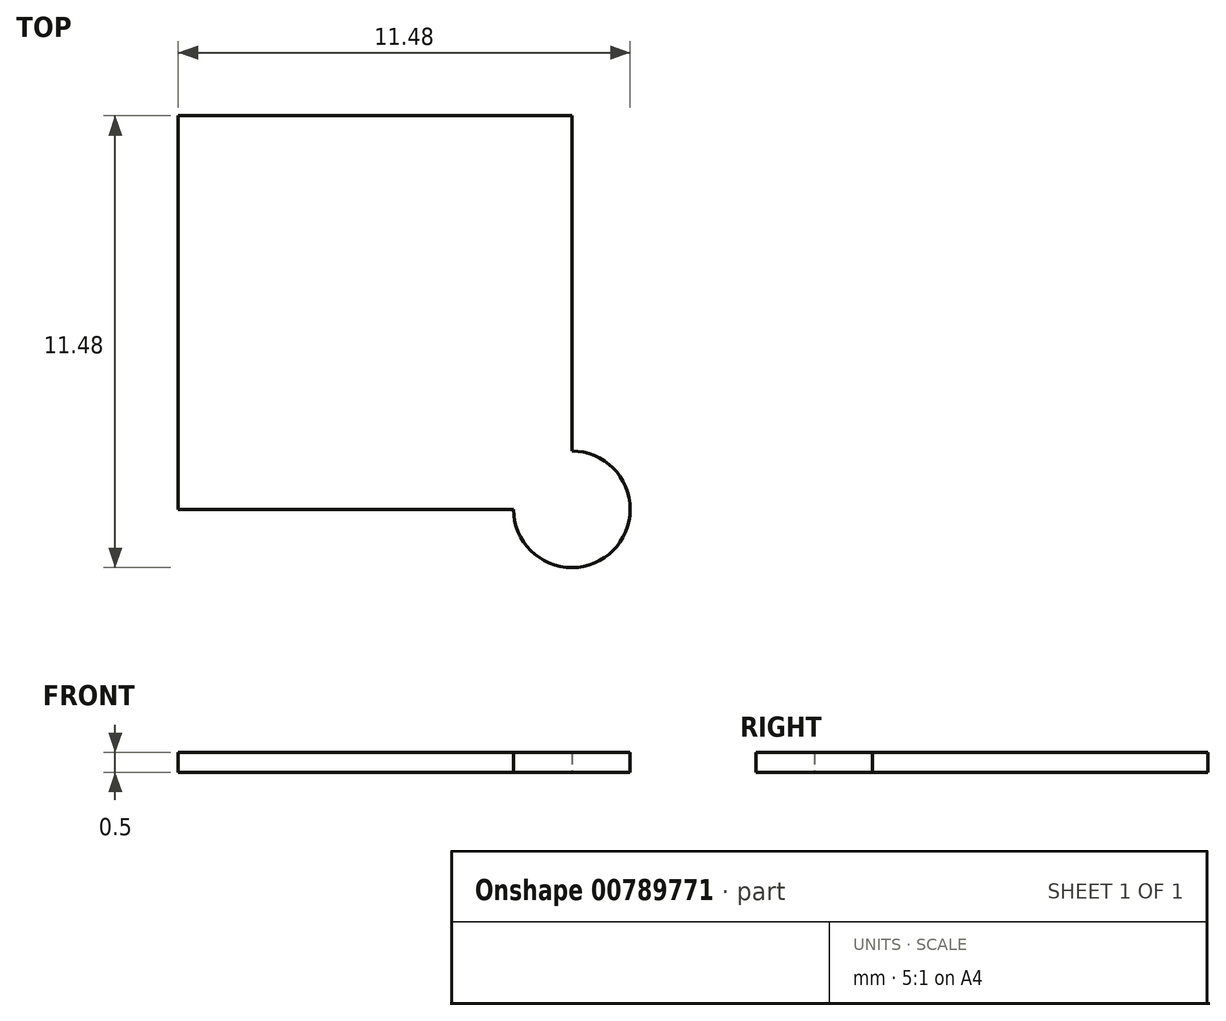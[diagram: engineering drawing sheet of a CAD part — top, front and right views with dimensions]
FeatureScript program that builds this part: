
annotation { "Feature Type Name" : "Feature", "Feature Type Description" : "" }
export const myFeature = defineFeature(function(context is Context, id is Id, definition is map)
    precondition{}
    {
        {
            var Q0;
            Q0=qCreatedBy(makeId("Top.planeOp"),FACE);
            var sketch = newSketch(context, id + "F0", { "sketchPlane" : qUnion([Q0])});
            skLineSegment(sketch, "E0.bottom", {"start": v(-10, 10) * mm, "end": v(0, 10) * mm});
            skLineSegment(sketch, "E0.top", {"start": v(-10, 0) * mm, "end": v(0, 0) * mm});
            skLineSegment(sketch, "E0.left", {"start": v(-10, 10) * mm, "end": v(-10, 0) * mm});
            skLineSegment(sketch, "E0.right", {"start": v(0, 10) * mm, "end": v(0, 0) * mm});
            skArc(sketch, "E1", {"start": v(-1.48, 0) * mm, "mid": v(1.05, -1.05) * mm, "end": v(0, 1.48) * mm});
            skSolve(sketch);
        }
        {
            var Q0;
            Q0=qSketchRegion(id+"F0",true);
            extrude(context, id + "F1", {"entities" : qUnion([Q0]), "depth" : 0.5 * mm, "offsetDistance" : 25 * mm});
        }
    });
